# Revit family: CS-212-15CP
name_source: partatom
category: Plumbing Fixtures
revit_build: Autodesk Revit Architecture 2012 (Build: 20110309_2315(x64)
units: mm (PartAtom-declared; Revit-internal decimal feet)

## types (2) — shared parameters
Default Elevation = 0' - 0"
Model = CS-212-15CP
Range = Capstan
Vent Connection = No
Waste Connection = No
zero-valued in all types: CWFU, Cost, HWFU, WFU

## per-type parameters (varying)
| type | 1/2" light pattern tap washer | Assembly Code | CW Connection | Connection backnut | Description | HW Connection | Headpart complete | Keynote | Manufacturer | Material | Type Comments | URL |
| Capstan |  |  | No |  |  | No |  |  |  |  |  |  |
| CS-212-15CP | C-098-15 | D2010 | Yes | 088-15 | Hot & cold indices included. 1/2"BSP male inlet | Yes | P-62-1CS/CP | Pillar tap | COBRA | Chrome - Polished | SANS 226 TYPE 2 | http://www.cobra.co.za |

## geometry (parser evidence)
native form markers: Blend x2
no freeform markers — native parametric forms only
